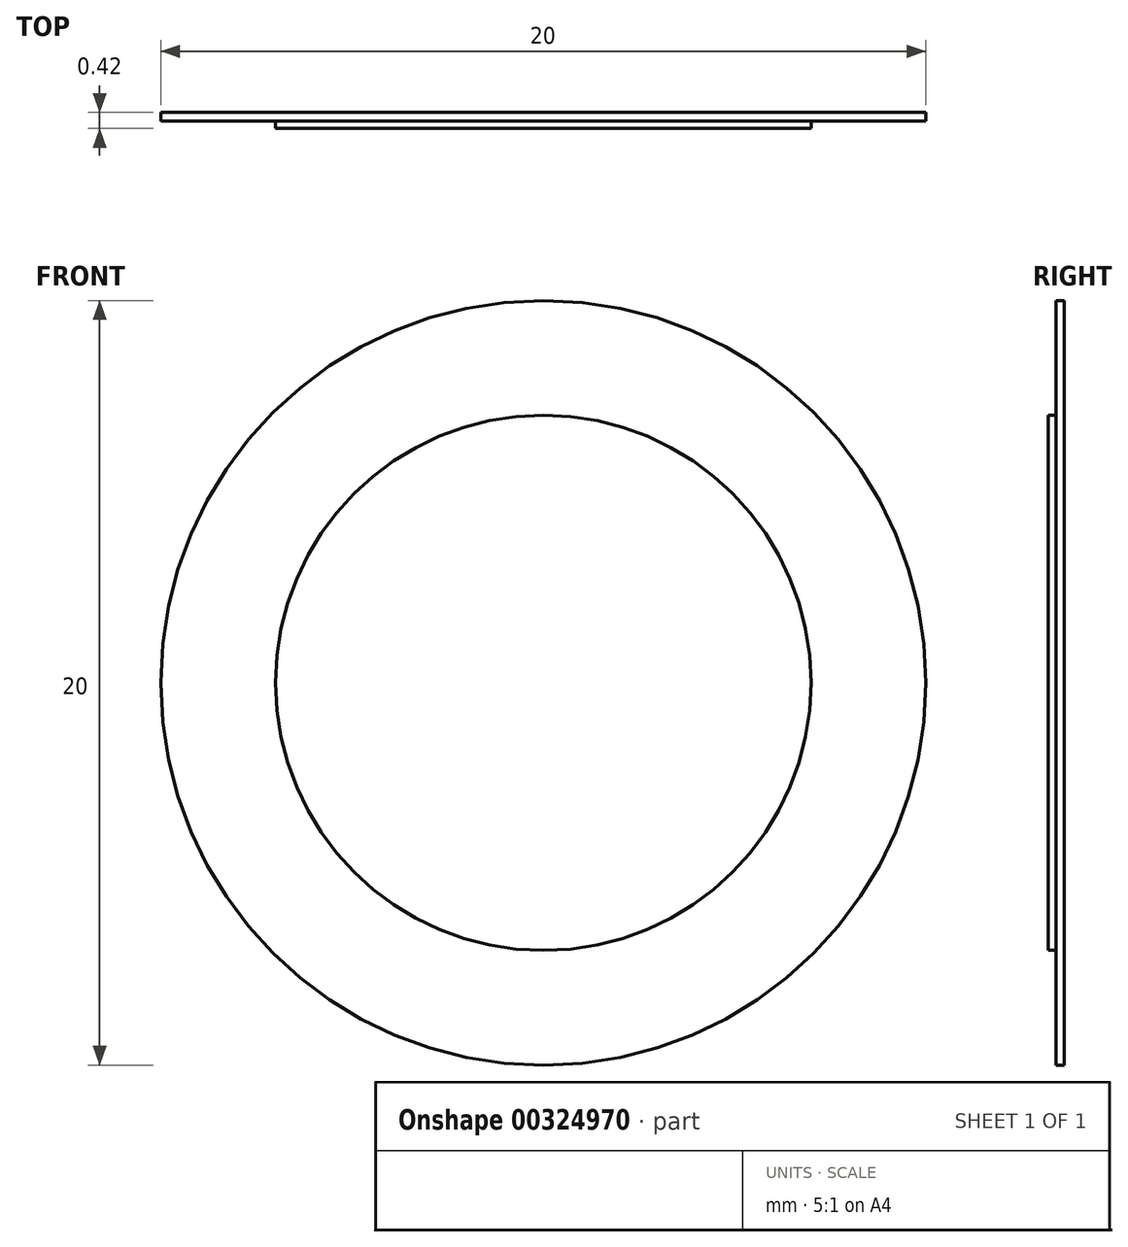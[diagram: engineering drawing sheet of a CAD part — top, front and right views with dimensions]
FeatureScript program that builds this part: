
annotation { "Feature Type Name" : "Feature", "Feature Type Description" : "" }
export const myFeature = defineFeature(function(context is Context, id is Id, definition is map)
    precondition{}
    {
        {
            var Q0;
            Q0=qCreatedBy(makeId("Front.planeOp"),FACE);
            var sketch = newSketch(context, id + "F0", { "sketchPlane" : qUnion([Q0])});
            skCircle(sketch, "E0", {"center": v(0, 0) * mm, "radius": 10 * mm});
            skCircle(sketch, "E1", {"center": v(0, 0) * mm, "radius": 7 * mm});
            skSolve(sketch);
        }
        {
            var Q0;
            Q0=makeQuery(id+"F0.imprint","IMPRINT",FACE,{"disambiguationData":[TD([[makeQuery(id+"F0.imprint","IMPRINT",EDGE,{"derivedFrom":sQuery(id+"F0.wireOp",EDGE,"E0")}),1.0]])]});
            var Q1;
            Q1=makeQuery(id+"F0.imprint","IMPRINT",FACE,{"disambiguationData":[TD([[makeQuery(id+"F0.imprint","IMPRINT",EDGE,{"derivedFrom":sQuery(id+"F0.wireOp",EDGE,"E1")}),1.0]])]});
            extrude(context, id + "F1", {"entities" : qUnion([Q0, Q1]), "oppositeDirection" : true, "depth" : .22 * mm});
        }
        {
            var Q0;
            Q0=makeQuery(id+"F0.imprint","IMPRINT",FACE,{"disambiguationData":[TD([[makeQuery(id+"F0.imprint","IMPRINT",EDGE,{"derivedFrom":sQuery(id+"F0.wireOp",EDGE,"E1")}),1.0]])]});
            extrude(context, id + "F2", {"entities" : qUnion([Q0]), "depth" : .2 * mm});
        }
    });
